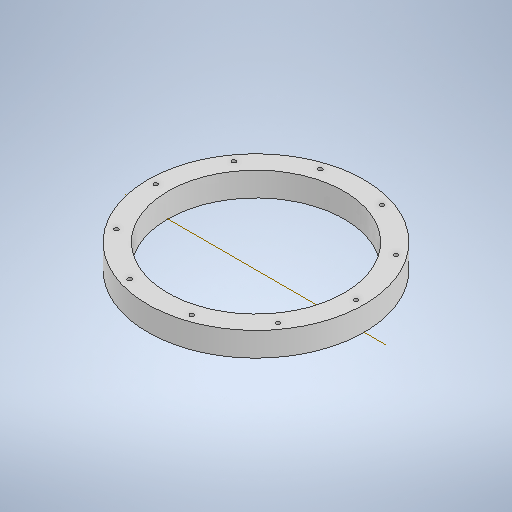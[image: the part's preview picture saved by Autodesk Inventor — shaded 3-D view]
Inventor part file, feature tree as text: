
AUTODESK INVENTOR PART (.ipt)
format: ipt  version: 2025 (Build 290162000, 162)  size: 246,784 bytes
history: native  units: in
note: dims shown in document units (in); Inventor stores cm internally (conversion verified against a paired STEP export)
features: sketch x2, extrude x1, hole x1, pattern_circular x1
ambient origin geometry x8: Origin, YZ Plane, XZ Plane, XY Plane, X Axis, Y Axis, Z Axis, Center Point
bodies: Solid1 (feature_tree)
feature tree (5):
  extrude  "Extrusion1"  Depth=8.6614in
  hole  "Hole1"  [1 undecoded]
  pattern_circular  "Circular Pattern1"  Count=10 Angle=360.0deg
  sketch  "Sketch1"  dims[d0=10.6299in d1=8.6614in]
  sketch  "Sketch2"  dims[d2=1.1811in d3=0.0in d4=0.2047in d5=0.2362in d6=0.1575in d7=0.0787in d8=90.0deg d9=0.315in d10=0.8108in d11=4.9213in d12=3.937in d13=360.0deg]
note: 1 required parameter value undecoded (feature->parameter linkage not recoverable at this tier; creation-order binding heuristic only, values carry confidence <= 0.55)
